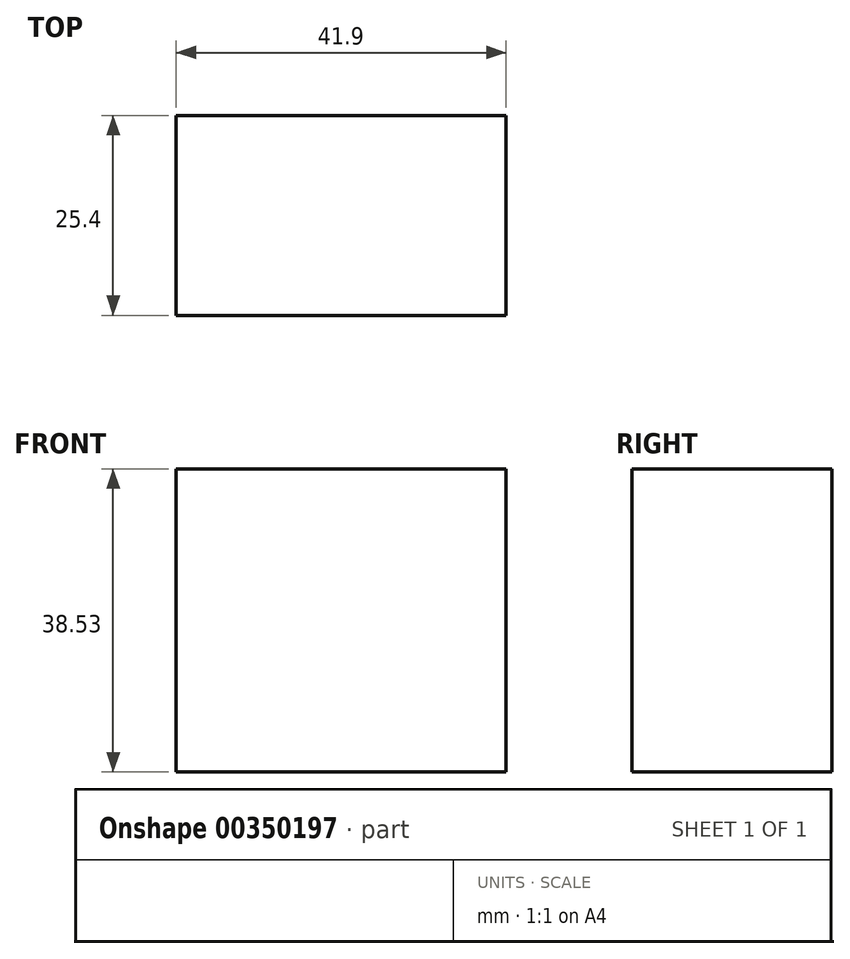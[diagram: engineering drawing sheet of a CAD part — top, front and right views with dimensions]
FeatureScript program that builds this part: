
annotation { "Feature Type Name" : "Feature", "Feature Type Description" : "" }
export const myFeature = defineFeature(function(context is Context, id is Id, definition is map)
    precondition{}
    {
        {
            var Q0;
            Q0=qCreatedBy(makeId("Front.planeOp"),FACE);
            var sketch = newSketch(context, id + "F0", { "sketchPlane" : qUnion([Q0])});
            skLineSegment(sketch, "E0.bottom", {"start": v(54.53, 0) * mm, "end": v(12.63, 0) * mm});
            skLineSegment(sketch, "E0.top", {"start": v(54.53, -38.53) * mm, "end": v(12.63, -38.53) * mm});
            skLineSegment(sketch, "E0.left", {"start": v(54.53, 0) * mm, "end": v(54.53, -38.53) * mm});
            skLineSegment(sketch, "E0.right", {"start": v(12.63, 0) * mm, "end": v(12.63, -38.53) * mm});
            skPoint(sketch, "E0.middle", {"position": v(33.58, -19.26) * mm});
            skSolve(sketch);
        }
        {
            var Q0;
            Q0=makeQuery(id+"F0.imprint","IMPRINT",FACE,{"disambiguationData":[TD([[makeQuery(id+"F0.imprint","IMPRINT",EDGE,{"derivedFrom":sQuery(id+"F0.wireOp",EDGE,"E0.bottom")}),1.0]])]});
            var Q1;
            Q1 = qSketchRegion(id + "F0", true);
            var Q2;
            Q2=sQuery(id+"F0.wireOp",EDGE,"E0.left");
            var Q3;
            Q3=sQuery(id+"F0.wireOp",EDGE,"E0.right");
            var Q4;
            Q4=sQuery(id+"F0.wireOp",EDGE,"E0.top");
            var Q5;
            Q5=sQuery(id+"F0.wireOp",EDGE,"E0.bottom");
            extrude(context, id + "F1", {"entities" : qUnion([Q0, Q1]), "bodyType" : ToolBodyType.SURFACE, "surfaceEntities" : qUnion([Q2, Q3, Q4, Q5]), "oppositeDirection" : true, "depth" : 25.4 * mm});
        }
    });
